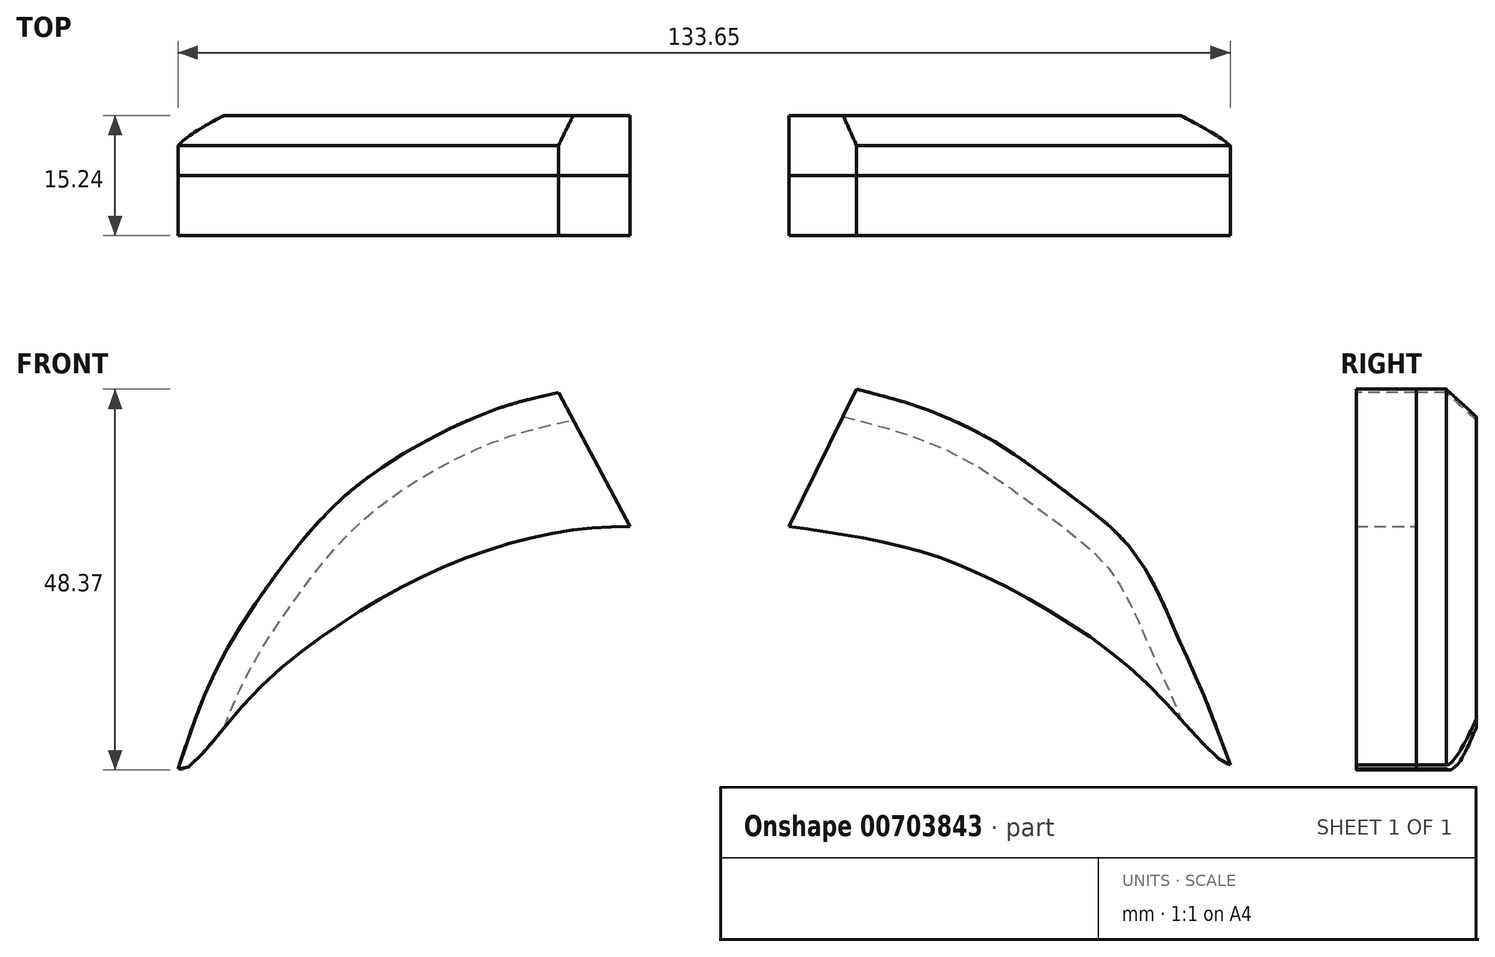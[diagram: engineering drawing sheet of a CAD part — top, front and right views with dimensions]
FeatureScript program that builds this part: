
annotation { "Feature Type Name" : "Feature", "Feature Type Description" : "" }
export const myFeature = defineFeature(function(context is Context, id is Id, definition is map)
    precondition{}
    {
        {
            var Q0;
            Q0=qCreatedBy(makeId("Front.planeOp"),FACE);
            var sketch = newSketch(context, id + "F0", { "sketchPlane" : qUnion([Q0])});
            skFitSpline(sketch, "E0", {"points": [v(28.63, 24.44) * mm, v(44.59, 14.28) * mm, v(54.56, 3.4) * mm, v(64, -14.2) * mm, v(66.17, -27.98) * mm, v(67.02, -42.39) * mm, v(58.4, -34.45) * mm, v(45.24, -23.86) * mm, v(30.95, -16.56) * mm, v(20.16, -13.67) * mm, v(10.58, -12.15) * mm], "startDerivative": vector(151.67, -87.38) * mm, "endDerivative": vector(-117, 17.02) * mm});
            skLineSegment(sketch, "E1", {"start": v(10.58, -12.15) * mm, "end": v(28.63, 24.44) * mm});
            skLineSegment(sketch, "E2", {"start": v(-29.18, 24.44) * mm, "end": v(-9.63, -12.15) * mm});
            skFitSpline(sketch, "E3", {"points": [v(-29.18, 24.44) * mm, v(-45.76, 13.42) * mm, v(-57.33, 0) * mm, v(-63.74, -13.63) * mm, v(-66.72, -29.43) * mm, v(-66.87, -43.03) * mm, v(-59.05, -35.22) * mm, v(-48.1, -25.68) * mm, v(-38.1, -19.58) * mm, v(-27.3, -15.04) * mm, v(-17.45, -12.7) * mm, v(-9.63, -12.15) * mm], "startDerivative": vector(-157.5, -92.28) * mm, "endDerivative": vector(109.56, 3.6) * mm});
            skSolve(sketch);
        }
        {
            var Q0;
            Q0=makeQuery(id+"F0.imprint","IMPRINT",FACE,{"disambiguationData":[TD([[makeQuery(id+"F0.imprint","IMPRINT",EDGE,{"derivedFrom":sQuery(id+"F0.wireOp",EDGE,"E2")}),-1.0]])]});
            var Q1;
            Q1=makeQuery(id+"F0.imprint","IMPRINT",FACE,{"disambiguationData":[TD([[makeQuery(id+"F0.imprint","IMPRINT",EDGE,{"derivedFrom":sQuery(id+"F0.wireOp",EDGE,"E0")}),-1.0]])]});
            extrude(context, id + "F1", {"entities" : qUnion([Q0, Q1]), "depth" : 7.62 * mm, "offsetDistance" : 25.4 * mm});
        }
        {
            var Q0;
            Q0=makeQuery(id+"F1.opExtrude","CAP_FACE",FACE,{"disambiguationData":[OSD([sQuery(id+"F0.wireOp",EDGE,"E2"),sQuery(id+"F0.wireOp",EDGE,"E3")])],"isStart":true});
            var Q1;
            Q1=makeQuery(id+"F1.opExtrude","CAP_FACE",FACE,{"disambiguationData":[OSD([sQuery(id+"F0.wireOp",EDGE,"E0"),sQuery(id+"F0.wireOp",EDGE,"E1")])],"isStart":true});
            extrude(context, id + "F2", {"entities" : qUnion([Q0, Q1]), "depth" : 7.62 * mm, "offsetDistance" : 25.4 * mm});
        }
        {
            var Q0;
            Q0=makeQuery(id+"F1.opExtrude","CAP_FACE",FACE,{"disambiguationData":[OSD([sQuery(id+"F0.wireOp",EDGE,"E2"),sQuery(id+"F0.wireOp",EDGE,"E3")])],"isStart":false});
            var sketch = newSketch(context, id + "F3", { "sketchPlane" : qUnion([Q0])});
            skFitSpline(sketch, "E4", {"points": [v(-18.71, 4.84) * mm, v(-27.4, 2.47) * mm, v(-39.68, -3.73) * mm, v(-48.13, -10.46) * mm, v(-54.97, -18.8) * mm, v(-62.09, -30.17) * mm, v(-67.02, -42.94) * mm], "startDerivative": vector(-56.78, -12.31) * mm, "endDerivative": vector(-24.22, -72.49) * mm});
            skSolve(sketch);
        }
        {
            var Q0;
            Q0=makeQuery(id+"F1.opExtrude","CAP_FACE",FACE,{"disambiguationData":[OSD([sQuery(id+"F0.wireOp",EDGE,"E0"),sQuery(id+"F0.wireOp",EDGE,"E1")])],"isStart":false});
            var sketch = newSketch(context, id + "F4", { "sketchPlane" : qUnion([Q0])});
            skFitSpline(sketch, "E5", {"points": [v(19.18, 5.3) * mm, v(29.27, 2.24) * mm, v(38.36, -2.44) * mm, v(45.81, -7.8) * mm, v(54.38, -15.43) * mm, v(59.93, -26.08) * mm, v(62.96, -32.83) * mm, v(66.63, -42.47) * mm], "startDerivative": vector(70, -18.2) * mm, "endDerivative": vector(26.01, -71.26) * mm});
            skSolve(sketch);
        }
        {
            var Q0;
            {var subQ0=sQuery(id+"F3.wireOp",EDGE,"E4");Q0=makeQuery(id+"F3.imprint","IMPRINT",FACE,{"disambiguationData":[TD([[makeQuery(id+"F3.imprint","IMPRINT",EDGE,{"derivedFrom":subQ0}),-1.0]])]});}
            extrude(context, id + "F5", {"entities" : qUnion([Q0]), "operationType" : NewBodyOperationType.REMOVE, "oppositeDirection" : true, "depth" : 25.4 * mm, "offsetDistance" : 25.4 * mm});
        }
        {
            var Q0;
            {var subQ0=sQuery(id+"F4.wireOp",EDGE,"E5");Q0=makeQuery(id+"F4.imprint","IMPRINT",FACE,{"disambiguationData":[TD([[makeQuery(id+"F4.imprint","IMPRINT",EDGE,{"derivedFrom":subQ0}),1.0]])]});}
            extrude(context, id + "F6", {"entities" : qUnion([Q0]), "operationType" : NewBodyOperationType.REMOVE, "oppositeDirection" : true, "depth" : 25.4 * mm, "offsetDistance" : 25.4 * mm});
        }
        {
            var Q0;
            Q0=makeQuery(id+"F5.boolean.opBoolean","COPY",EDGE,{"derivedFrom":makeQuery(id+"F5.opExtrude","CAP_EDGE",EDGE,{"disambiguationData":[OSD([sQuery(id+"F3.wireOp",EDGE,"E4")])],"isStart":true})});
            var Q1;
            Q1=makeQuery(id+"F6.boolean.opBoolean","COPY",EDGE,{"derivedFrom":makeQuery(id+"F6.opExtrude","CAP_EDGE",EDGE,{"disambiguationData":[OSD([sQuery(id+"F4.wireOp",EDGE,"E5")])],"isStart":true})});
            var Q2;
            Q2=makeQuery(id+"F5.boolean.opBoolean","INTERSECT",EDGE,{"derivedFrom":[makeQuery(id+"F2.opExtrude","CAP_FACE",FACE,{"disambiguationData":[OSD([sQuery(id+"F0.wireOp",EDGE,"E2"),sQuery(id+"F0.wireOp",EDGE,"E3")])],"isStart":false}),makeQuery(id+"F5.opExtrude","SWEPT_FACE",FACE,{"disambiguationData":[OSD([sQuery(id+"F3.wireOp",EDGE,"E4")])]})]});
            var Q3;
            Q3=makeQuery(id+"F6.boolean.opBoolean","INTERSECT",EDGE,{"derivedFrom":[makeQuery(id+"F2.opExtrude","CAP_FACE",FACE,{"disambiguationData":[OSD([sQuery(id+"F0.wireOp",EDGE,"E0"),sQuery(id+"F0.wireOp",EDGE,"E1")])],"isStart":false}),makeQuery(id+"F6.opExtrude","SWEPT_FACE",FACE,{"disambiguationData":[OSD([sQuery(id+"F4.wireOp",EDGE,"E5")])]})]});
            chamfer(context, id + "F7", {"entities" : qUnion([Q0, Q1, Q2, Q3]), "width" : 3.8 * mm, "tangentPropagation" : true});
        }
    });
